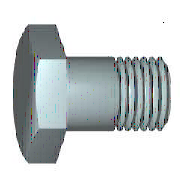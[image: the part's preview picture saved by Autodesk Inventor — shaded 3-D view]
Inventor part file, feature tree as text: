
AUTODESK INVENTOR PART (.ipt)
format: ipt  version: 2014 SP1 (Build 180222100, 222)  size: 187,392 bytes
history: native  units: mm (DEFAULTED — no unit token found)
features: sketch x3, extrude x2, chamfer x1, fillet x1, plane x1
ambient origin geometry x7: Origin, YZ Plane, XZ Plane, X Axis, Y Axis, Z Axis, Center Point
bodies: Solid1 (feature_tree), Body (feature_tree)
feature tree (8):
  extrude  "Head"  TaperAngle=90.0deg  [1 undecoded]
  chamfer  "Chamfer1"  Angle=90.0deg  [1 undecoded]
  fillet  "Fillet2"  Radius=0.61345mm
  plane  "Work Plane1"
  extrude  "Extrusion5"  Depth=0.25mm
  sketch  "Sketch1"  dims[d2=6.0mm d12=90.0deg]
  sketch  "Sketch2"  dims[d3=4.0mm]
  sketch  "Sketch7"  dims[d4=0.0mm d21=90.0deg d6=0.61345mm d7=0.61355mm d8=0.0mm d11=10.0mm d15=19.0mm d16=0.0mm d55=45.0deg d58=0.0mm d59=20.0mm d65=10.0mm d67=30.0deg d68=12.0mm d69=4.0mm d71=0.25mm d73=0.0mm d74=1.0mm d75=0.0mm]
note: 2 required parameter values undecoded (feature->parameter linkage not recoverable at this tier; creation-order binding heuristic only, values carry confidence <= 0.55)
